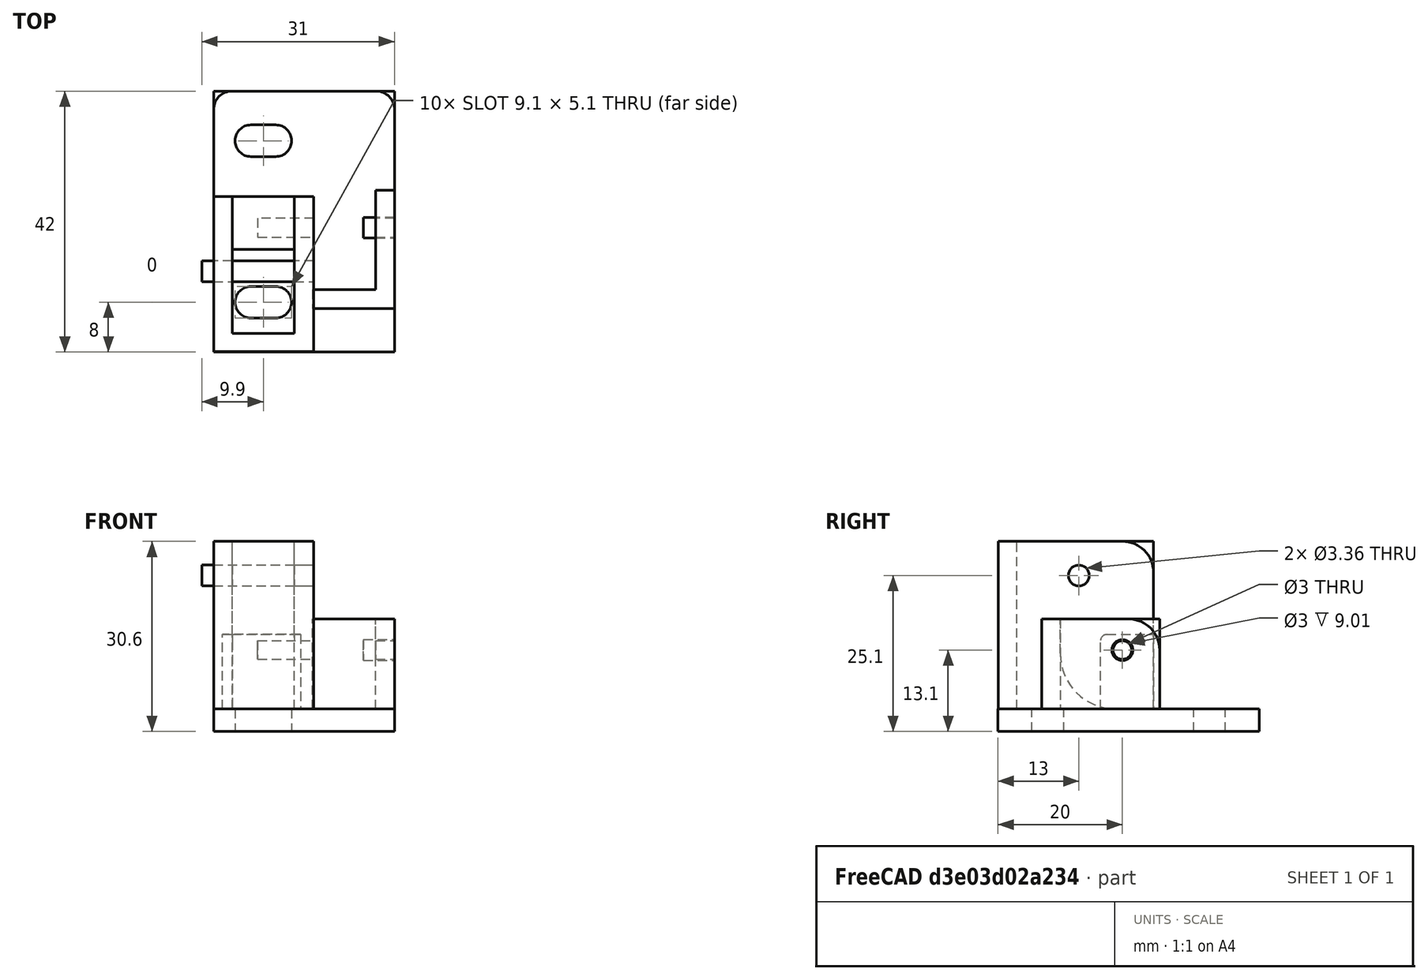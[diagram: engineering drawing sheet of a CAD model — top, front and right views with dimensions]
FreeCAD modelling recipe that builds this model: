
FCSTD DOCUMENT  (FreeCAD 0.16R6706 (Git))
Label: belt-junction
License: All rights reserved
LicenseURL: http://en.wikipedia.org/wiki/All_rights_reserved
objects: Sketcher::SketchObject×7, PartDesign::Pocket×4, PartDesign::Fillet×4, PartDesign::Pad×3, Mesh::Feature×2, Part::Box×1
note: 26 computed .brp shape members not serialized (recipe doc carries the construction recipe); baked Part::Feature solids carry a one-line shape summary decoded from their .brp

FEATURE [Part::Box] Box  label="Cube"
  Height = 3.6
  Length = 29.1
  Width = 42
FEATURE [Sketcher::SketchObject] Sketch001  label="mnt holes"
  Placement = pos=(0,0,0) rot=(1,0,0;3.14159rad)
  Support = -> Box [Face5]
  sketch-geometry (8):
    g0: ArcOfCircle CenterX=10 CenterY=-34 CenterZ=0 NormalX=0 NormalY=0 NormalZ=1 Radius=2.55 StartAngle=4.71239 EndAngle=7.85398
    g1: ArcOfCircle CenterX=6 CenterY=-34 CenterZ=0 NormalX=0 NormalY=0 NormalZ=1 Radius=2.55 StartAngle=1.5708 EndAngle=4.71239
    g2: LineSegment StartX=10 StartY=-31.45 StartZ=0 EndX=6 EndY=-31.45 EndZ=0
    g3: LineSegment StartX=10 StartY=-36.55 StartZ=0 EndX=6 EndY=-36.55 EndZ=0
    g4: ArcOfCircle CenterX=10 CenterY=-8 CenterZ=0 NormalX=0 NormalY=0 NormalZ=1 Radius=2.55 StartAngle=4.71239 EndAngle=7.85398
    g5: ArcOfCircle CenterX=6 CenterY=-8 CenterZ=0 NormalX=0 NormalY=0 NormalZ=1 Radius=2.55 StartAngle=1.5708 EndAngle=4.71239
    g6: LineSegment StartX=10 StartY=-5.45 StartZ=0 EndX=6 EndY=-5.45 EndZ=0
    g7: LineSegment StartX=10 StartY=-10.55 StartZ=0 EndX=6 EndY=-10.55 EndZ=0
  constraints (20):
    c: Tangent(g0,g3) = 1.5708
    c: Tangent(g0,g2) = -1.5708
    c: Tangent(g2,g1) = -1.5708
    c: Tangent(g3,g1) = 1.5708
    c: Horizontal(g2)
    c: Equal(g0,g1)
    c: Tangent(g4,g7) = 1.5708
    c: Tangent(g4,g6) = -1.5708
    c: Tangent(g6,g5) = -1.5708
    c: Tangent(g7,g5) = 1.5708
    c: Horizontal(g6)
    c: Equal(g4,g5)
    c: Distance(g4,g4) = 5.1
    c: DistanceY(g-1,g5) = -8
    c: DistanceX(g-2,g5) = 6
    c: Distance(g4,g5) = 4
    c: Distance(g0,g1) = 4
    c: Distance(g0,g0) = 5.1
    c: DistanceX(g-2,g1) = 6
    c: Distance(g0,g4) = 26
FEATURE [PartDesign::Pocket] Pocket
  Length = 5
  Sketch = -> Sketch001
  Type = 0
FEATURE [PartDesign::Fillet] Fillet
  Base = -> Pocket [Edge3,Edge19]
  Radius = 3
FEATURE [Sketcher::SketchObject] Sketch  label="btm frame"
  Placement = pos=(0,0,3.6) rot=(0,0,1;0rad)
  Support = -> Fillet [Face2]
  sketch-geometry (6):
    g0: LineSegment StartX=29.09 StartY=7 StartZ=0 EndX=29.09 EndY=26 EndZ=0
    g1: LineSegment StartX=29.09 StartY=26 StartZ=0 EndX=26.09 EndY=26 EndZ=0
    g2: LineSegment StartX=26.09 StartY=26 StartZ=0 EndX=26.09 EndY=10 EndZ=0
    g3: LineSegment StartX=26.09 StartY=10 StartZ=0 EndX=15.9078 EndY=10 EndZ=0
    g4: LineSegment StartX=15.9078 StartY=10 StartZ=0 EndX=15.9078 EndY=7 EndZ=0
    g5: LineSegment StartX=15.9078 StartY=7 StartZ=0 EndX=29.09 EndY=7 EndZ=0
  constraints (17):
    c: Coincident(g0,g1)
    c: Coincident(g1,g2)
    c: Coincident(g2,g3)
    c: Coincident(g3,g4)
    c: Coincident(g4,g5)
    c: Coincident(g5,g0)
    c: Parallel(g2,g0)
    c: Parallel(g0,g4)
    c: Parallel(g4,g-2)
    c: Parallel(g3,g5)
    c: Parallel(g5,g1)
    c: Parallel(g1,g-1)
    c: Distance(g1) = 3
    c: Equal(g4,g1)
    c: DistanceY(g0) = 7
    c: DistanceY(g0) = 26
    c: DistanceX(g0) = 29.09
FEATURE [PartDesign::Pad] Pad
  Length = 14.5
  Length2 = 100
  Sketch = -> Sketch
  Type = 0
FEATURE [Sketcher::SketchObject] Sketch003  label="top frame"
  Placement = pos=(0,0,3.6) rot=(0,0,1;0rad)
  Support = -> Pad [Face8]
  sketch-geometry (8):
    g0: LineSegment StartX=0 StartY=25 StartZ=0 EndX=0 EndY=0.05 EndZ=0
    g1: LineSegment StartX=0 StartY=0.05 StartZ=0 EndX=16.1 EndY=0.05 EndZ=0
    g2: LineSegment StartX=16.1 StartY=0.05 StartZ=0 EndX=16.1 EndY=25 EndZ=0
    g3: LineSegment StartX=16.1 StartY=25 StartZ=0 EndX=13 EndY=25 EndZ=0
    g4: LineSegment StartX=13 StartY=25 StartZ=0 EndX=13 EndY=3 EndZ=0
    g5: LineSegment StartX=13 StartY=3 StartZ=0 EndX=3 EndY=3 EndZ=0
    g6: LineSegment StartX=3 StartY=3 StartZ=0 EndX=3 EndY=25 EndZ=0
    g7: LineSegment StartX=3 StartY=25 StartZ=0 EndX=0 EndY=25 EndZ=0
  constraints (23):
    c: Coincident(g0,g1)
    c: Coincident(g1,g2)
    c: Coincident(g2,g3)
    c: Coincident(g3,g4)
    c: Coincident(g4,g5)
    c: Coincident(g5,g6)
    c: Coincident(g6,g7)
    c: Coincident(g7,g0)
    c: Parallel(g1,g3)
    c: Parallel(g3,g5)
    c: Parallel(g5,g7)
    c: Parallel(g7,g-1)
    c: Parallel(g0,g6)
    c: Parallel(g6,g4)
    c: Parallel(g4,g2)
    c: Parallel(g2,g-2)
    c: Distance(g7) = 3
    c: Distance(g5) = 10
    c: DistanceY(g1) = 0.05
    c: DistanceX(g0) = 0
    c: DistanceY(g4) = 3
    c: Distance(g3) = 3.1
    c: DistanceY(g2) = 25
FEATURE [PartDesign::Pad] Pad001
  Length = 27
  Length2 = 100
  Sketch = -> Sketch003
  Type = 0
FEATURE [Mesh::Feature] davebot_initial_layout  label="btm pulley"
  Placement = pos=(11.5,188.2,-120.1) rot=(0,1,0;1.5708rad)
FEATURE [Mesh::Feature] davebot_initial_layout001  label="top pulley"
  Placement = pos=(24.5,194.2,-132.1) rot=(0,1,0;1.5708rad)
FEATURE [Sketcher::SketchObject] Sketch005
  Placement = pos=(0,0,3.6) rot=(0,0,1;0rad)
  Support = -> Pad001 [Face3]
  sketch-geometry (4):
    g0: LineSegment StartX=14 StartY=25.0245 StartZ=0 EndX=1.4 EndY=25.0245 EndZ=0
    g1: LineSegment StartX=1.4 StartY=25.0245 StartZ=0 EndX=1.4 EndY=16.4844 EndZ=0
    g2: LineSegment StartX=1.4 StartY=16.4844 StartZ=0 EndX=14 EndY=16.4844 EndZ=0
    g3: LineSegment StartX=14 StartY=16.4844 StartZ=0 EndX=14 EndY=25.0245 EndZ=0
  constraints (8):
    c: Coincident(g0,g1)
    c: Coincident(g1,g2)
    c: Coincident(g2,g3)
    c: Coincident(g3,g0)
    c: Horizontal(g0)
    c: Horizontal(g2)
    c: Vertical(g1)
    c: Vertical(g3)
FEATURE [PartDesign::Pad] Pad002
  Length = 12
  Length2 = 100
  Sketch = -> Sketch005
  Type = 0
FEATURE [PartDesign::Fillet] Fillet001
  Base = -> Pad002 [Edge86]
  Radius = 1
FEATURE [Sketcher::SketchObject] Sketch004  label="top axel"
  Placement = pos=(16.1,0,0) rot=(0.57735,0.57735,0.57735;2.0944rad)
  Support = -> Fillet001 [Face16]
  sketch-geometry (1):
    g0: Circle CenterX=13 CenterY=25.1 CenterZ=0 NormalX=0 NormalY=0 NormalZ=1 Radius=1.68
  constraints (3):
    c: Radius(g0) = 1.68
    c: DistanceX(g0) = 13
    c: DistanceY(g0) = 25.1
FEATURE [PartDesign::Pocket] Pocket001
  Length = 18
  Sketch = -> Sketch004
  Type = 0
FEATURE [Sketcher::SketchObject] Sketch002  label="btm axel"
  Placement = pos=(29.09,0,0) rot=(0.57735,0.57735,0.57735;2.0944rad)
  Support = -> Pocket001 [Face26]
  sketch-geometry (1):
    g0: Circle CenterX=20 CenterY=13.1 CenterZ=0 NormalX=0 NormalY=0 NormalZ=1 Radius=1.5
  constraints (3):
    c: Radius(g0) = 1.5
    c: DistanceY(g-1,g0) = 13.1
    c: DistanceX(g-2,g0) = 20
FEATURE [PartDesign::Pocket] Pocket002
  Length = 22
  Sketch = -> Sketch002
  Type = 0
FEATURE [PartDesign::Fillet] Fillet002
  Base = -> Pocket002 [Edge56]
  Radius = 9
FEATURE [PartDesign::Fillet] Fillet003
  Base = -> Fillet002 [Edge33,Edge48,Edge64]
  Radius = 5
FEATURE [Sketcher::SketchObject] Sketch006
  Placement = pos=(29.09,0,0) rot=(0.57735,0.57735,0.57735;2.0944rad)
  Support = -> Fillet003 [Face9]
  sketch-geometry (1):
    g0: Circle CenterX=20 CenterY=13.1 CenterZ=0 NormalX=0 NormalY=0 NormalZ=1 Radius=1.68
  constraints (3):
    c: DistanceY(g0) = 13.1
    c: DistanceX(g0) = 20
    c: Radius(g0) = 1.68
FEATURE [PartDesign::Pocket] Pocket003
  Length = 5
  Sketch = -> Sketch006
  Type = 0
